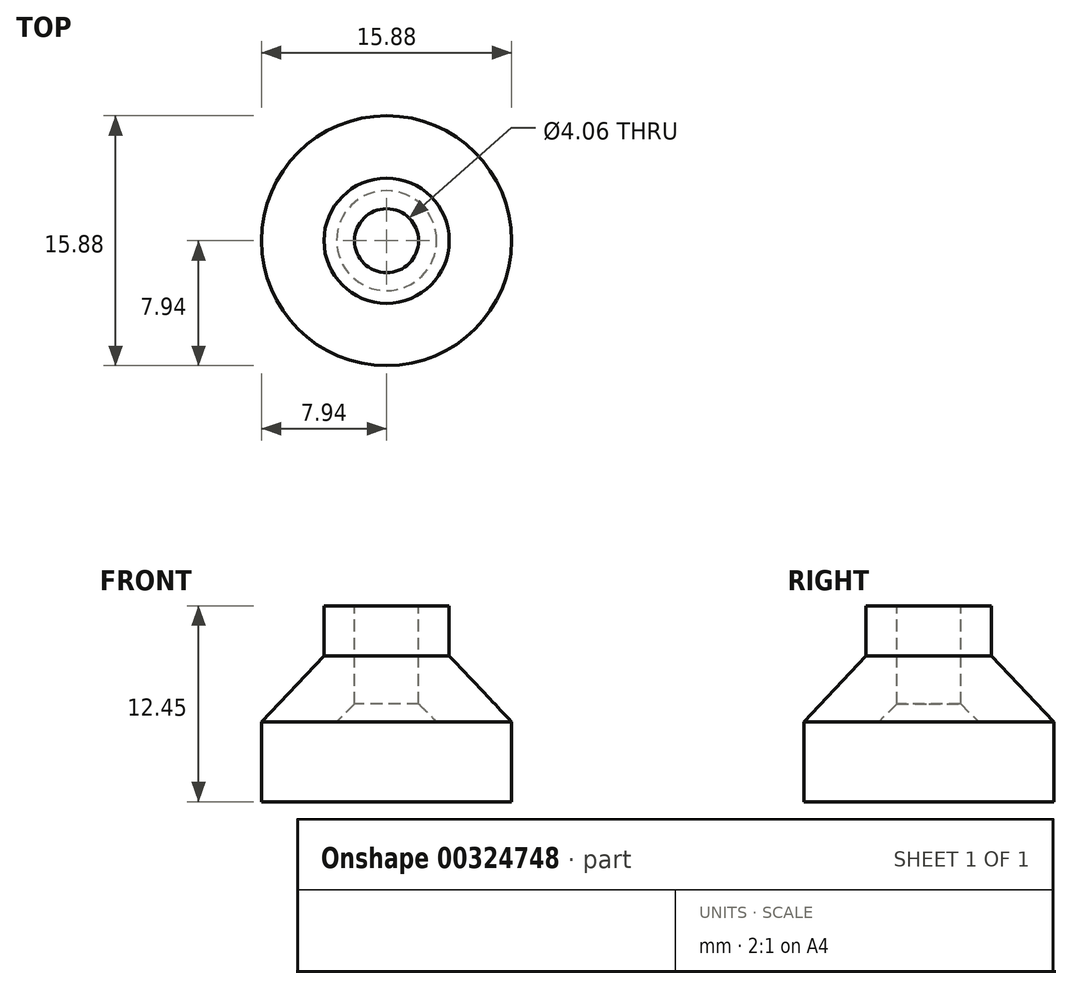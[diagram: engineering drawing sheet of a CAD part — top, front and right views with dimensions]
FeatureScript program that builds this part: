
annotation { "Feature Type Name" : "Feature", "Feature Type Description" : "" }
export const myFeature = defineFeature(function(context is Context, id is Id, definition is map)
    precondition{}
    {
        {
            var Q0;
            Q0=qCreatedBy(makeId("Top.planeOp"),FACE);
            var sketch = newSketch(context, id + "F0", { "sketchPlane" : qUnion([Q0])});
            skCircle(sketch, "E0", {"center": v(0, 0) * mm, "radius": 7.94 * mm});
            skSolve(sketch);
        }
        {
            var Q0;
            Q0=makeQuery(id+"F0.imprint","IMPRINT",FACE,{"disambiguationData":[TD([[makeQuery(id+"F0.imprint","IMPRINT",EDGE,{"derivedFrom":sQuery(id+"F0.wireOp",EDGE,"E0")}),1.0]])]});
            extrude(context, id + "F1", {"entities" : qUnion([Q0]), "depth" : 5.08 * mm, "offsetDistance" : 25.4 * mm});
        }
        {
            var Q0;
            Q0=qCreatedBy(makeId("Front.planeOp"),FACE);
            var sketch = newSketch(context, id + "F2", { "sketchPlane" : qUnion([Q0])});
            skLineSegment(sketch, "E1", {"start": v(0, 5.08) * mm, "end": v(7.94, 5.08) * mm});
            skLineSegment(sketch, "E2", {"start": v(7.94, 5.08) * mm, "end": v(3.98, 9.27) * mm});
            skLineSegment(sketch, "E3", {"start": v(3.98, 9.27) * mm, "end": v(0, 9.27) * mm});
            skLineSegment(sketch, "E4", {"start": v(0, 9.27) * mm, "end": v(0, 5.08) * mm});
            skSolve(sketch);
        }
        {
            var Q0;
            Q0=makeQuery(id+"F2.imprint","IMPRINT",FACE,{"disambiguationData":[TD([[makeQuery(id+"F2.imprint","IMPRINT",EDGE,{"derivedFrom":sQuery(id+"F2.wireOp",EDGE,"E1")}),1.0]])]});
            var Q1;
            Q1=makeQuery(id+"F1.opExtrude","CAP_EDGE",EDGE,{"disambiguationData":[OSD([sQuery(id+"F0.wireOp",EDGE,"E0")])],"isStart":false});
            sweep(context, id + "F3", {"profiles" : qUnion([Q0]), "path" : qUnion([Q1])});
        }
        {
            var Q0;
            Q0=makeQuery(id+"F3.opSweep","SWEPT_FACE",FACE,{"disambiguationData":[OSD([sQuery(id+"F0.wireOp",EDGE,"E0"),sQuery(id+"F2.wireOp",EDGE,"E3")])]});
            var sketch = newSketch(context, id + "F4", { "sketchPlane" : qUnion([Q0])});
            skCircle(sketch, "E5", {"center": v(0, 0) * mm, "radius": 3.98 * mm});
            skSolve(sketch);
        }
        {
            var Q0;
            Q0=makeQuery(id+"F4.imprint","IMPRINT",FACE,{"disambiguationData":[TD([[makeQuery(id+"F4.imprint","IMPRINT",EDGE,{"derivedFrom":sQuery(id+"F4.wireOp",EDGE,"E5")}),1.0]])]});
            extrude(context, id + "F5", {"entities" : qUnion([Q0]), "operationType" : NewBodyOperationType.ADD, "depth" : 3.17 * mm, "offsetDistance" : 25.4 * mm});
        }
        {
            var Q0;
            Q0=makeQuery(id+"F1.opExtrude","CAP_FACE",FACE,{"disambiguationData":[OSD([sQuery(id+"F0.wireOp",EDGE,"E0")])],"isStart":true});
            var sketch = newSketch(context, id + "F6", { "sketchPlane" : qUnion([Q0])});
            skSolve(sketch);
        }
        {
            var Q0;
            Q0=makeQuery(id+"F6.imprint","IMPRINT",FACE,{"disambiguationData":[TD([[makeQuery(id+"F6.imprint","IMPRINT",EDGE,{"derivedFrom":makeQuery(id+"F1.opExtrude","CAP_EDGE",EDGE,{"disambiguationData":[OSD([sQuery(id+"F0.wireOp",EDGE,"E0")])],"isStart":true})}),-1.0]])]});
            var sketch = newSketch(context, id + "F7", { "sketchPlane" : qUnion([Q0])});
            skPoint(sketch, "E6", {"position": v(0, 0) * mm});
            skSolve(sketch);
        }
        {
            var Q0;
            Q0=sQuery(id+"F7.wireOp",VERTEX,"E6");
            var Q1;
            Q1=makeQuery(id+"F3.opSweep","SWEPT_BODY",BODY,{"disambiguationData":[OSD([sQuery(id+"F0.wireOp",EDGE,"E0"),sQuery(id+"F2.wireOp",EDGE,"E1"),sQuery(id+"F2.wireOp",EDGE,"E2"),sQuery(id+"F2.wireOp",EDGE,"E3"),sQuery(id+"F2.wireOp",EDGE,"E4")])]});
            hole(context, id + "F8", {"style" : HoleStyle.C_SINK, "endStyle" : HoleEndStyle.THROUGH, "holeDiameter" : 4.06 * mm, "cSinkDiameter" : 6.35 * mm, "cSinkAngle" : 90 * degree, "majorDiameter" : 6.35 * mm, "tappedDepth" : 12.7 * mm, "tapClearance" : 3, "locations" : qUnion([Q0]), "scope" : qUnion([Q1])});
        }
    });
